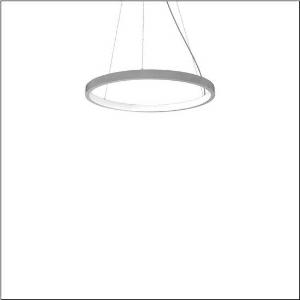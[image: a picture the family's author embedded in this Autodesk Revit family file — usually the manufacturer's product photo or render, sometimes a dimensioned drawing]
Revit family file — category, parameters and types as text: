
# Revit family: silica_r__21_ring-i_5pjbi2d3204a_c88e
name_source: partatom
category: Lighting Fixtures
units: mm (PartAtom-declared; Revit-internal decimal feet)

## family parameters
Cut with Voids When Loaded = No
Host = Face
Light Source = No
Part Type = Normal
Room Calculation Point = No
Round Connector Dimension = Use Diameter
Shared = No

## types (1)
- Silica® 21 Ring-I (1 x LED, 5040 lm, 80 W, 4000K)
    Apparent Load = 80 VA
    CIE Flux Codes = 22 48 76 50 101
    Color Rendering = 80
    Color Temperature = 4000K
    Default Elevation = 1800 mm
    Description = Silica® 21 Ring-I, suspended luminaire, of PMMA, frosted, light emission: inner ring side luminous distribution, primary light characteristic: symmetric, installation type: suspended mounting, LED, rated luminous flux: 5.040lm, luminous efficacy: 63lm/W, light colour: 840, colour temperature: 4000K, control gear: DALI 2, with terminal, 5-pole, mains connection: 230V, AC/DC, 0/50..60Hz, rated input power: 80W, housing, of extruded aluminium section, metallic grey (RAL 9006), diameter: 805mm, ceiling canopy, metallic grey (RAL 9006), protection rating (lamp compartment): IP40, insulation class (complete): insulation class I (protective earthing), certification: CE, impact resistance: IK02, permissible operating ambient temperature: 0..+35°C, packaging unit: 1 piece
    Height = 48 mm  [stored 0.15748 ft]
    Lamp = 1 x LED
    Lamp Light Flux = 5040 lm
    Lamp Power = 80 W
    Lamp count = 1
    Length = 805 mm
    Luminous efficacy = 63 lm/W
    Manufacturer = Siteco
    ModVariant = No
    Model = 5PJBI2D3204A
    Mounting Place = Ceiling
    Mounting Type = Pendant
    Number of Poles = 1
    OnlyDefault = Yes
    Power Factor = 1
    Product Name = Silica® 21 Ring-I
    Product group = suspended luminaire
    ProductGroupID = 905
    Protection Class = Protection class I
    Protection Degree = IP 40
    RLX_Detail_Level = 1
    RLX_Emergency_Light_Flux = 0 lm
    RLX_Emergency_Type = 0
    RLX_Emergency_Type_DB = No
    RlxData = <blob elided: 13125 chars, md5=8347fd84>
    Socket = socket
    Standby Power = 0 W
    System Light Flux = 5040 lm
    System Power = 80 W
    Type Comments = Product without accessories
    Type Image = l_1251752.jpg
    URL = http://relux.com
    VarID = ---
    Voltage = 0 V
    Weight = 0.00 kg
    Width = 0 mm  [stored 0 ft]

note: [stored X ft] marks values corroborated as IEEE doubles in the binary element streams (Revit-internal decimal feet)

## geometry (parser evidence)
native form markers: Sweep x11
no freeform markers — native parametric forms only
